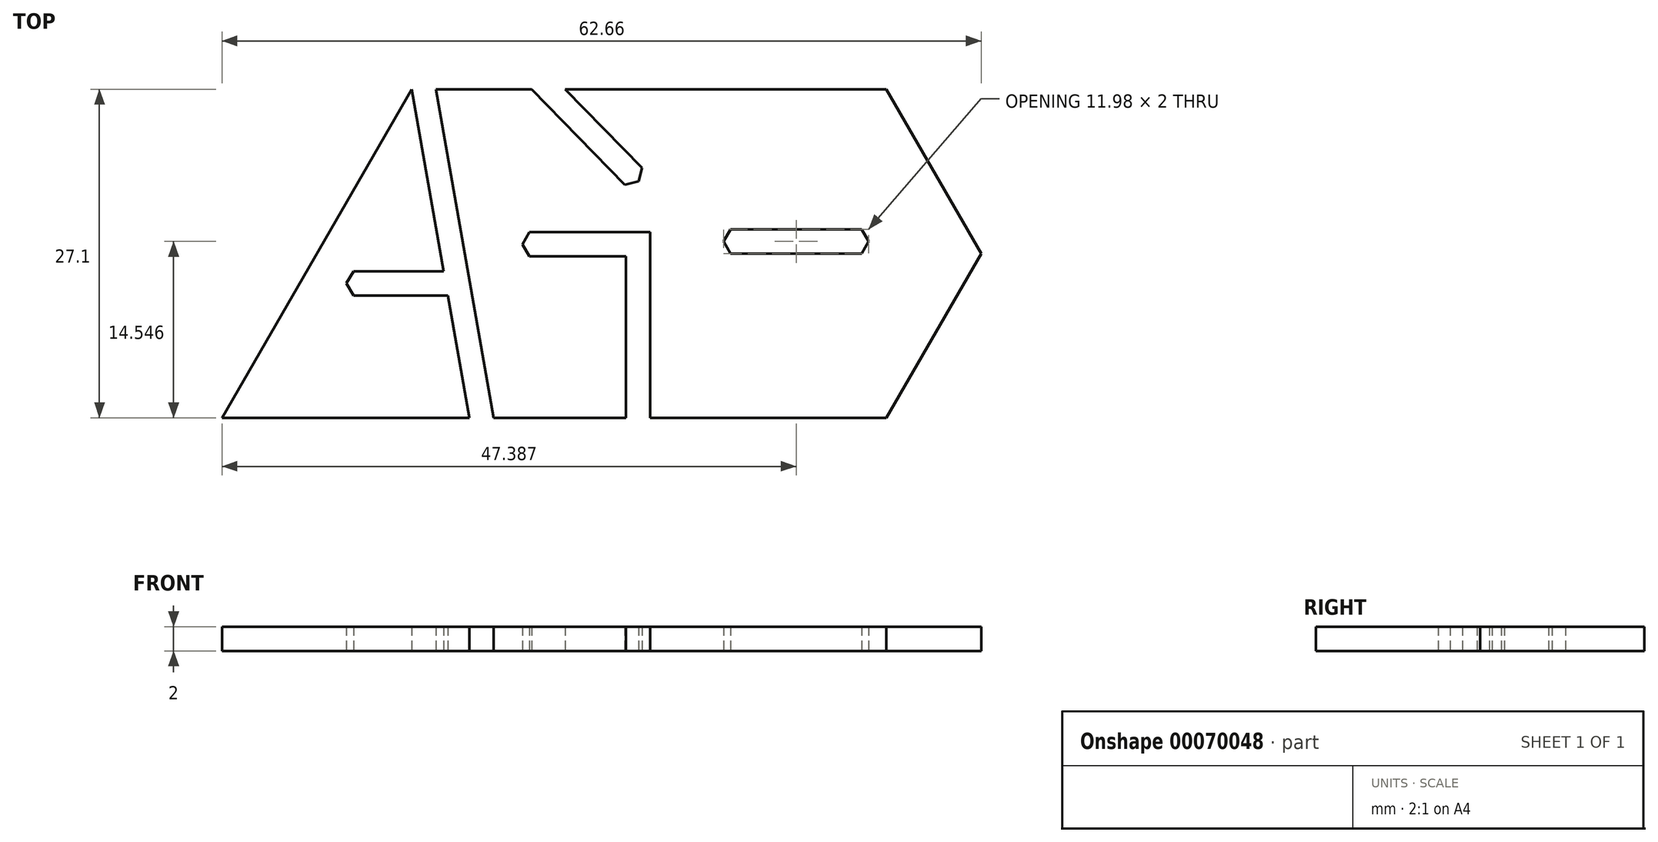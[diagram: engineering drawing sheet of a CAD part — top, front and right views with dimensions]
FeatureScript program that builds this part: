
annotation { "Feature Type Name" : "Feature", "Feature Type Description" : "" }
export const myFeature = defineFeature(function(context is Context, id is Id, definition is map)
    precondition{}
    {
        {
            var Q0;
            Q0=qCreatedBy(makeId("Top.planeOp"),FACE);
            var sketch = newSketch(context, id + "F0", { "sketchPlane" : qUnion([Q0])});
            skLineSegment(sketch, "E0", {"start": v(-34.91, -14.38) * mm, "end": v(-14.49, -14.38) * mm});
            skLineSegment(sketch, "E1", {"start": v(-14.49, -14.38) * mm, "end": v(-19.26, 12.72) * mm});
            skLineSegment(sketch, "E2", {"start": v(-19.26, 12.72) * mm, "end": v(-34.91, -14.38) * mm});
            skLineSegment(sketch, "E3", {"start": v(-16.27, -4.3) * mm, "end": v(-24.07, -4.3) * mm});
            skLineSegment(sketch, "E4", {"start": v(-14.49, -14.38) * mm, "end": v(19.93, -14.38) * mm});
            skLineSegment(sketch, "E5", {"start": v(-19.26, 12.72) * mm, "end": v(19.93, 12.72) * mm});
            skLineSegment(sketch, "E6", {"start": v(19.93, -14.38) * mm, "end": v(27.75, -0.83) * mm});
            skLineSegment(sketch, "E7", {"start": v(27.75, -0.83) * mm, "end": v(19.93, 12.72) * mm});
            skLineSegment(sketch, "E8", {"start": v(17.89, -0.83) * mm, "end": v(7.07, -0.83) * mm});
            skPoint(sketch, "E9.endSnap0", {"position": v(-16.88, -0.83) * mm});
            skLineSegment(sketch, "E10.0", {"start": v(-20.42, 14.72) * mm, "end": v(21.08, 14.72) * mm});
            skLineSegment(sketch, "E10.1", {"start": v(-38.38, -16.38) * mm, "end": v(-14.97, -16.38) * mm});
            skLineSegment(sketch, "E10.2", {"start": v(-14.97, -16.38) * mm, "end": v(21.08, -16.38) * mm});
            skLineSegment(sketch, "E10.3", {"start": v(-20.42, 14.72) * mm, "end": v(-38.38, -16.38) * mm});
            skLineSegment(sketch, "E10.4", {"start": v(21.08, -16.38) * mm, "end": v(30.06, -0.83) * mm});
            skLineSegment(sketch, "E11", {"start": v(-24.07, -2.3) * mm, "end": v(-16.62, -2.3) * mm});
            skLineSegment(sketch, "E12", {"start": v(-17.26, 12.72) * mm, "end": v(-12.49, -14.38) * mm});
            skLineSegment(sketch, "E13", {"start": v(-19.26, 12.72) * mm, "end": v(-17.26, 12.72) * mm});
            skLineSegment(sketch, "E14", {"start": v(0.42, -14.38) * mm, "end": v(-1.58, -14.38) * mm});
            skLineSegment(sketch, "E15", {"start": v(-1.58, -14.38) * mm, "end": v(-1.58, -1.07) * mm});
            skLineSegment(sketch, "E16", {"start": v(-9.55, -1.07) * mm, "end": v(-1.58, -1.07) * mm});
            skLineSegment(sketch, "E17", {"start": v(7.07, 1.17) * mm, "end": v(17.89, 1.17) * mm});
            skLineSegment(sketch, "E18", {"start": v(0.42, -14.38) * mm, "end": v(0.42, 0.93) * mm});
            skLineSegment(sketch, "E19", {"start": v(0.42, 0.93) * mm, "end": v(-9.55, 0.93) * mm});
            skLineSegment(sketch, "E20", {"start": v(-1.66, 4.84) * mm, "end": v(-9.34, 12.72) * mm});
            skLineSegment(sketch, "E21", {"start": v(-24.07, -4.3) * mm, "end": v(-24.64, -3.3) * mm});
            skLineSegment(sketch, "E22", {"start": v(-24.64, -3.3) * mm, "end": v(-24.07, -2.3) * mm});
            skLineSegment(sketch, "E23", {"start": v(-9.55, -1.07) * mm, "end": v(-10.12, -0.07) * mm});
            skLineSegment(sketch, "E24", {"start": v(-10.12, -0.07) * mm, "end": v(-9.55, 0.93) * mm});
            skLineSegment(sketch, "E25", {"start": v(-0.23, 6.23) * mm, "end": v(-6.6, 12.72) * mm});
            skLineSegment(sketch, "E26", {"start": v(-1.66, 4.84) * mm, "end": v(-0.54, 5.12) * mm});
            skLineSegment(sketch, "E27", {"start": v(-0.54, 5.12) * mm, "end": v(-0.23, 6.23) * mm});
            skLineSegment(sketch, "E28", {"start": v(7.07, 1.17) * mm, "end": v(6.49, 0.17) * mm});
            skLineSegment(sketch, "E29", {"start": v(6.49, 0.17) * mm, "end": v(7.07, -0.83) * mm});
            skLineSegment(sketch, "E30", {"start": v(17.89, 1.17) * mm, "end": v(18.47, 0.17) * mm});
            skLineSegment(sketch, "E31", {"start": v(18.47, 0.17) * mm, "end": v(17.89, -0.83) * mm});
            skLineSegment(sketch, "E32", {"start": v(30.06, -0.83) * mm, "end": v(39.04, 14.72) * mm});
            skLineSegment(sketch, "E33", {"start": v(21.08, 14.72) * mm, "end": v(39.04, 14.72) * mm});
            skLineSegment(sketch, "E34", {"start": v(28.9, 1.17) * mm, "end": v(35.58, 12.72) * mm});
            skLineSegment(sketch, "E35", {"start": v(28.9, 1.17) * mm, "end": v(22.24, 12.72) * mm});
            skLineSegment(sketch, "E36", {"start": v(22.24, 12.72) * mm, "end": v(35.58, 12.72) * mm});
            skSolve(sketch);
        }
        {
            var Q0;
            {var subQ6=sQuery(id+"F0.wireOp",EDGE,"E6");Q0=makeQuery(id+"F0.imprint","IMPRINT",FACE,{"disambiguationData":[TD([[makeQuery(id+"F0.imprint","IMPRINT",EDGE,{"derivedFrom":subQ6}),1.0]])]});}
            var Q1;
            {var subQ3=sQuery(id+"F0.wireOp",EDGE,"E0");Q1=makeQuery(id+"F0.imprint","IMPRINT",FACE,{"disambiguationData":[TD([[makeQuery(id+"F0.imprint","IMPRINT",EDGE,{"derivedFrom":subQ3}),1.0]])]});}
            extrude(context, id + "F1", {"entities" : qUnion([Q0, Q1]), "depth" : 2 * mm});
        }
    });
